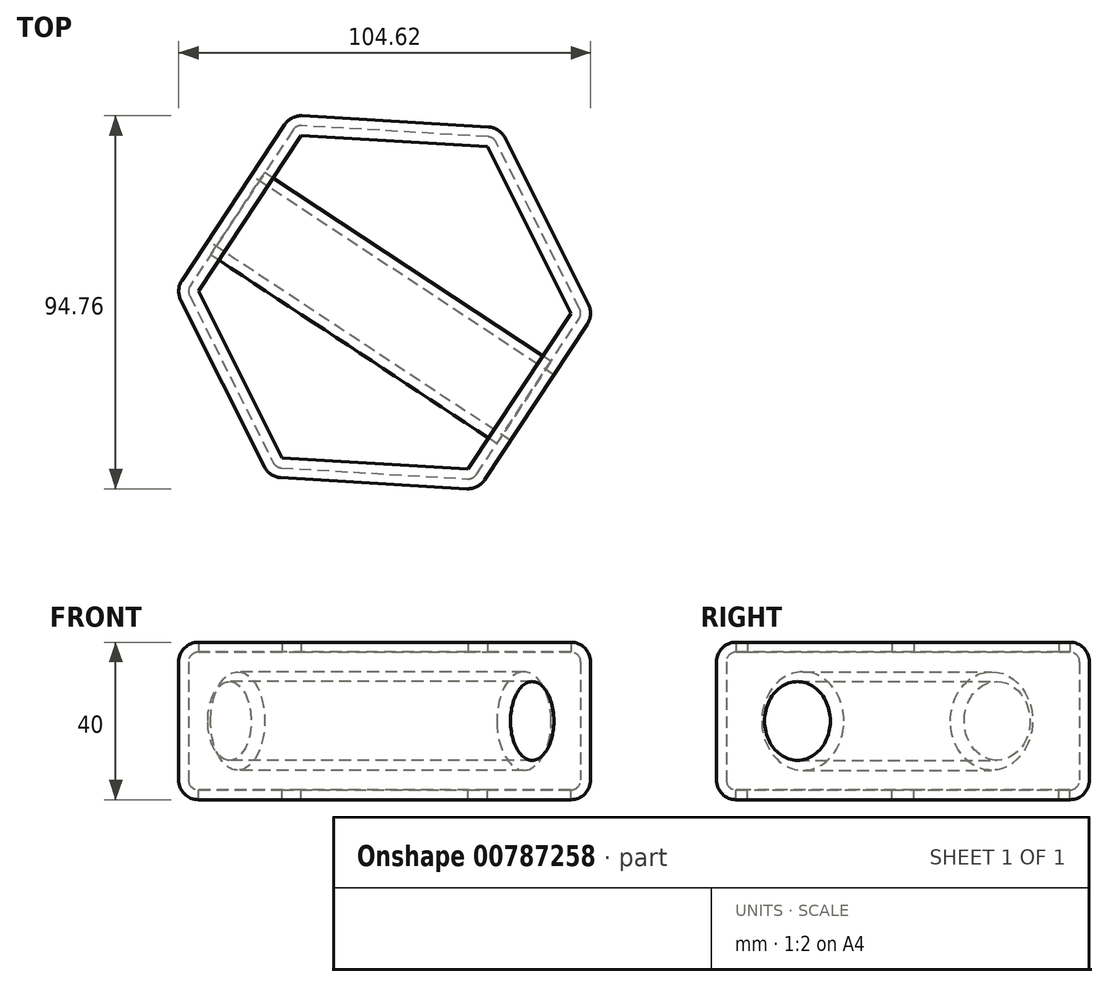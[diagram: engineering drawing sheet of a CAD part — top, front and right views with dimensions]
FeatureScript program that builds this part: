
annotation { "Feature Type Name" : "Feature", "Feature Type Description" : "" }
export const myFeature = defineFeature(function(context is Context, id is Id, definition is map)
    precondition{}
    {
        {
            var Q0;
            Q0=qCreatedBy(makeId("Top.planeOp"),FACE);
            var sketch = newSketch(context, id + "F0", { "sketchPlane" : qUnion([Q0])});
            skCircle(sketch, "E0.cCircle", {"center": v(0, 0) * mm, "radius": 46.05 * mm, "construction": true});
            skLineSegment(sketch, "E0.0", {"start": v(-23.8, 47.55) * mm, "end": v(29.27, 44.39) * mm});
            skLineSegment(sketch, "E0.1", {"start": v(29.27, 44.39) * mm, "end": v(53.08, -3.16) * mm});
            skLineSegment(sketch, "E0.2", {"start": v(53.08, -3.16) * mm, "end": v(23.8, -47.55) * mm});
            skLineSegment(sketch, "E0.3", {"start": v(23.8, -47.55) * mm, "end": v(-29.27, -44.39) * mm});
            skLineSegment(sketch, "E0.4", {"start": v(-29.27, -44.39) * mm, "end": v(-53.08, 3.16) * mm});
            skLineSegment(sketch, "E0.5", {"start": v(-53.08, 3.16) * mm, "end": v(-23.8, 47.55) * mm});
            skPoint(sketch, "E0.0.midPoint", {"position": v(2.73, 45.97) * mm});
            skSolve(sketch);
        }
        {
            var Q0;
            Q0=makeQuery(id+"F0.imprint","IMPRINT",FACE,{"disambiguationData":[TD([[makeQuery(id+"F0.imprint","IMPRINT",EDGE,{"derivedFrom":sQuery(id+"F0.wireOp",EDGE,"E0.0")}),-1.0]])]});
            extrude(context, id + "F1", {"entities" : qUnion([Q0]), "depth" : 40 * mm, "offsetDistance" : 25 * mm});
        }
        {
            var Q0;
            Q0=makeQuery(id+"F1.opExtrude","CAP_EDGE",EDGE,{"disambiguationData":[OSD([sQuery(id+"F0.wireOp",EDGE,"E0.0")])],"isStart":false});
            var Q1;
            Q1=makeQuery(id+"F1.opExtrude","CAP_EDGE",EDGE,{"disambiguationData":[OSD([sQuery(id+"F0.wireOp",EDGE,"E0.1")])],"isStart":false});
            var Q2;
            Q2=makeQuery(id+"F1.opExtrude","CAP_EDGE",EDGE,{"disambiguationData":[OSD([sQuery(id+"F0.wireOp",EDGE,"E0.2")])],"isStart":false});
            var Q3;
            Q3=makeQuery(id+"F1.opExtrude","CAP_EDGE",EDGE,{"disambiguationData":[OSD([sQuery(id+"F0.wireOp",EDGE,"E0.3")])],"isStart":false});
            var Q4;
            Q4=makeQuery(id+"F1.opExtrude","CAP_EDGE",EDGE,{"disambiguationData":[OSD([sQuery(id+"F0.wireOp",EDGE,"E0.4")])],"isStart":false});
            var Q5;
            Q5=makeQuery(id+"F1.opExtrude","CAP_EDGE",EDGE,{"disambiguationData":[OSD([sQuery(id+"F0.wireOp",EDGE,"E0.5")])],"isStart":false});
            var Q6;
            Q6=makeQuery(id+"F1.opExtrude","SWEPT_EDGE",EDGE,{"disambiguationData":[OSD([sQuery(id+"F0.wireOp",EDGE,"E0.0"),sQuery(id+"F0.wireOp",EDGE,"E0.1")])]});
            var Q7;
            Q7=makeQuery(id+"F1.opExtrude","SWEPT_EDGE",EDGE,{"disambiguationData":[OSD([sQuery(id+"F0.wireOp",EDGE,"E0.0"),sQuery(id+"F0.wireOp",EDGE,"E0.5")])]});
            var Q8;
            Q8=makeQuery(id+"F1.opExtrude","SWEPT_EDGE",EDGE,{"disambiguationData":[OSD([sQuery(id+"F0.wireOp",EDGE,"E0.4"),sQuery(id+"F0.wireOp",EDGE,"E0.5")])]});
            var Q9;
            Q9=makeQuery(id+"F1.opExtrude","SWEPT_EDGE",EDGE,{"disambiguationData":[OSD([sQuery(id+"F0.wireOp",EDGE,"E0.3"),sQuery(id+"F0.wireOp",EDGE,"E0.4")])]});
            var Q10;
            Q10=makeQuery(id+"F1.opExtrude","SWEPT_EDGE",EDGE,{"disambiguationData":[OSD([sQuery(id+"F0.wireOp",EDGE,"E0.2"),sQuery(id+"F0.wireOp",EDGE,"E0.3")])]});
            var Q11;
            Q11=makeQuery(id+"F1.opExtrude","SWEPT_EDGE",EDGE,{"disambiguationData":[OSD([sQuery(id+"F0.wireOp",EDGE,"E0.1"),sQuery(id+"F0.wireOp",EDGE,"E0.2")])]});
            var Q12;
            Q12=makeQuery(id+"F1.opExtrude","CAP_EDGE",EDGE,{"disambiguationData":[OSD([sQuery(id+"F0.wireOp",EDGE,"E0.1")])],"isStart":true});
            var Q13;
            Q13=makeQuery(id+"F1.opExtrude","CAP_EDGE",EDGE,{"disambiguationData":[OSD([sQuery(id+"F0.wireOp",EDGE,"E0.2")])],"isStart":true});
            var Q14;
            Q14=makeQuery(id+"F1.opExtrude","CAP_EDGE",EDGE,{"disambiguationData":[OSD([sQuery(id+"F0.wireOp",EDGE,"E0.3")])],"isStart":true});
            var Q15;
            Q15=makeQuery(id+"F1.opExtrude","CAP_EDGE",EDGE,{"disambiguationData":[OSD([sQuery(id+"F0.wireOp",EDGE,"E0.4")])],"isStart":true});
            var Q16;
            Q16=makeQuery(id+"F1.opExtrude","CAP_EDGE",EDGE,{"disambiguationData":[OSD([sQuery(id+"F0.wireOp",EDGE,"E0.5")])],"isStart":true});
            var Q17;
            Q17=makeQuery(id+"F1.opExtrude","CAP_EDGE",EDGE,{"disambiguationData":[OSD([sQuery(id+"F0.wireOp",EDGE,"E0.0")])],"isStart":true});
            fillet(context, id + "F2", {"entities" : qUnion([Q0, Q1, Q2, Q3, Q4, Q5, Q6, Q7, Q8, Q9, Q10, Q11, Q12, Q13, Q14, Q15, Q16, Q17]), "radius" : 5 * mm, "tangentPropagation" : true, "allowEdgeOverflow" : false});
        }
        {
            var Q0;
            Q0=makeQuery(id+"F1.opExtrude","SWEPT_FACE",FACE,{"disambiguationData":[OSD([sQuery(id+"F0.wireOp",EDGE,"E0.5")])]});
            var sketch = newSketch(context, id + "F3", { "sketchPlane" : qUnion([Q0])});
            skCircle(sketch, "E1", {"center": v(1.75, 20) * mm, "radius": 4.63 * mm});
            skPoint(sketch, "E1.centerSnap0", {"position": v(23.7, 20) * mm});
            skSolve(sketch);
        }
        {
            var Q0;
            Q0=sQuery(id+"F3.wireOp",VERTEX,"E1.center");
            var Q1;
            Q1=makeQuery(id+"F1.opExtrude","SWEPT_BODY",BODY,{"disambiguationData":[OSD([sQuery(id+"F0.wireOp",EDGE,"E0.0"),sQuery(id+"F0.wireOp",EDGE,"E0.1"),sQuery(id+"F0.wireOp",EDGE,"E0.2"),sQuery(id+"F0.wireOp",EDGE,"E0.3"),sQuery(id+"F0.wireOp",EDGE,"E0.4"),sQuery(id+"F0.wireOp",EDGE,"E0.5")])]});
            hole(context, id + "F4", {"style" : HoleStyle.C_BORE, "endStyle" : HoleEndStyle.THROUGH, "holeDiameter" : 20 * mm, "cBoreDiameter" : 20 * mm, "cBoreDepth" : 20 * mm, "majorDiameter" : 5 * mm, "isTappedThrough" : true, "tappedDepth" : 12 * mm, "tapClearance" : 3, "startFromSketch" : true, "locations" : qUnion([Q0]), "scope" : qUnion([Q1])});
        }
        {
            var Q0;
            Q0=makeQuery(id+"F1.opExtrude","CAP_FACE",FACE,{"disambiguationData":[OSD([sQuery(id+"F0.wireOp",EDGE,"E0.0"),sQuery(id+"F0.wireOp",EDGE,"E0.1"),sQuery(id+"F0.wireOp",EDGE,"E0.2"),sQuery(id+"F0.wireOp",EDGE,"E0.3"),sQuery(id+"F0.wireOp",EDGE,"E0.4"),sQuery(id+"F0.wireOp",EDGE,"E0.5")])],"isStart":true});
            var Q1;
            Q1=makeQuery(id+"F1.opExtrude","CAP_FACE",FACE,{"disambiguationData":[OSD([sQuery(id+"F0.wireOp",EDGE,"E0.0"),sQuery(id+"F0.wireOp",EDGE,"E0.1"),sQuery(id+"F0.wireOp",EDGE,"E0.2"),sQuery(id+"F0.wireOp",EDGE,"E0.3"),sQuery(id+"F0.wireOp",EDGE,"E0.4"),sQuery(id+"F0.wireOp",EDGE,"E0.5")])],"isStart":false});
            shell(context, id + "F5", {"entities" : qUnion([Q0, Q1]), "thickness" : 2.5 * mm});
        }
    });
